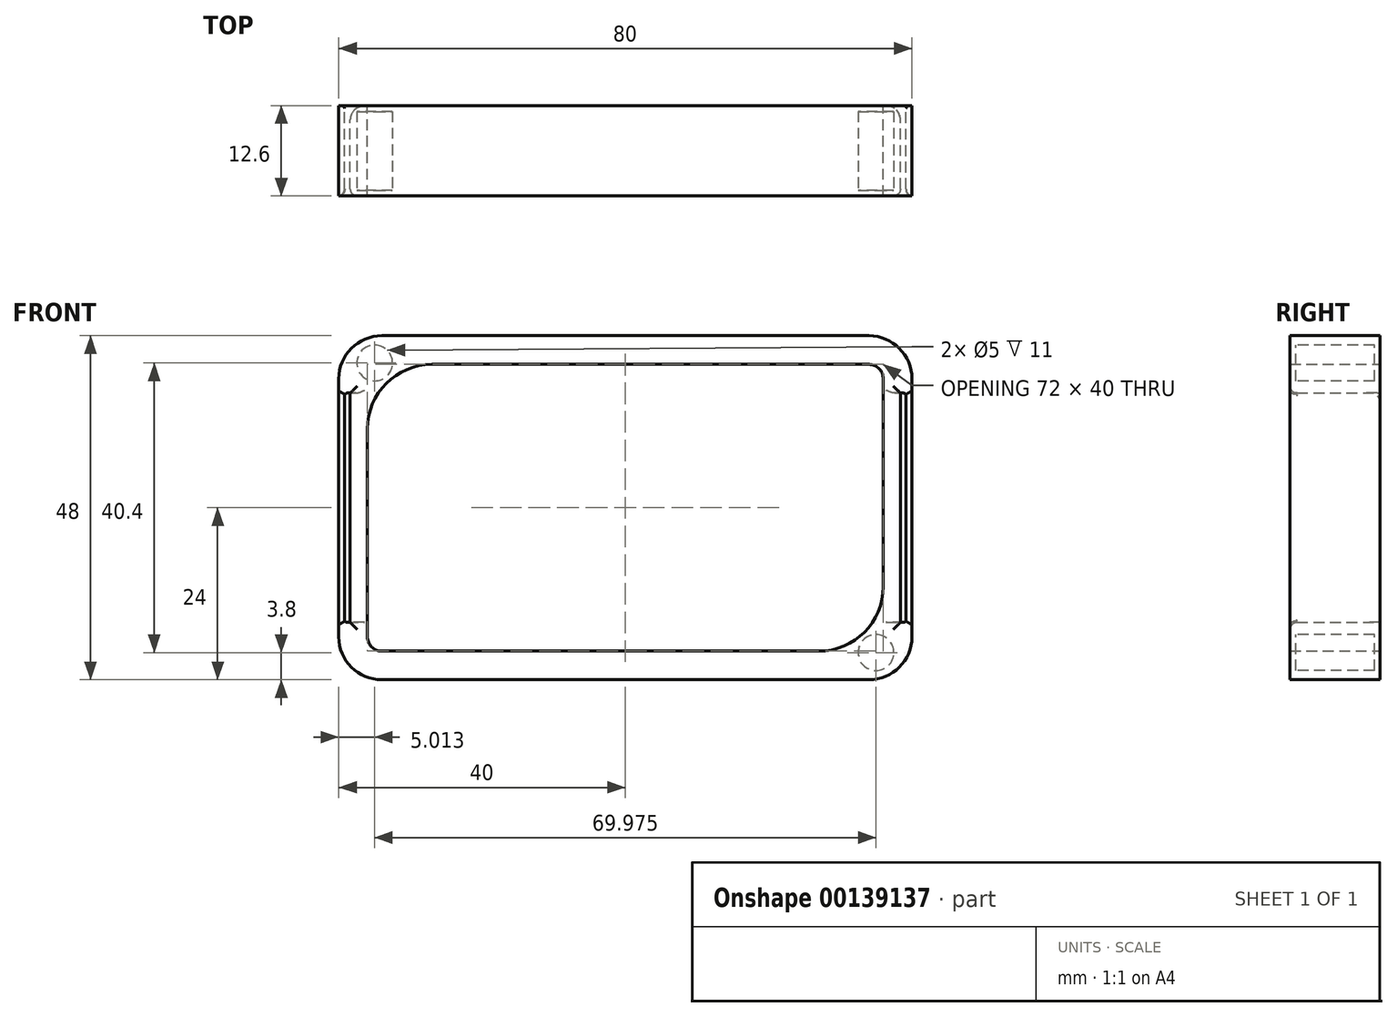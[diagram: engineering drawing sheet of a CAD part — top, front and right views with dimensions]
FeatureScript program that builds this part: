
annotation { "Feature Type Name" : "Feature", "Feature Type Description" : "" }
export const myFeature = defineFeature(function(context is Context, id is Id, definition is map)
    precondition{}
    {
        {
            var Q0;
            Q0=qCreatedBy(makeId("Front.planeOp"),FACE);
            var sketch = newSketch(context, id + "F0", { "sketchPlane" : qUnion([Q0])});
            skLineSegment(sketch, "E0.bottom", {"start": v(-34, 24) * mm, "end": v(34, 24) * mm});
            skLineSegment(sketch, "E0.top", {"start": v(-34, -24) * mm, "end": v(34, -24) * mm});
            skLineSegment(sketch, "E0.left", {"start": v(-40, 18) * mm, "end": v(-40, -18) * mm});
            skLineSegment(sketch, "E0.right", {"start": v(40, 18) * mm, "end": v(40, -18) * mm});
            skPoint(sketch, "E1", {"position": v(0, 24) * mm});
            skPoint(sketch, "E2", {"position": v(-40, 0) * mm});
            skPoint(sketch, "E3.visualSharp", {"position": v(-40, 24) * mm});
            skArc(sketch, "E3.filletArc", {"start": v(-34, 24) * mm, "mid": v(-38.24, 22.24) * mm, "end": v(-40, 18) * mm});
            skPoint(sketch, "E4.visualSharp", {"position": v(40, 24) * mm});
            skArc(sketch, "E4.filletArc", {"start": v(40, 18) * mm, "mid": v(38.24, 22.24) * mm, "end": v(34, 24) * mm});
            skPoint(sketch, "E5.visualSharp", {"position": v(40, -24) * mm});
            skArc(sketch, "E5.filletArc", {"start": v(34, -24) * mm, "mid": v(38.24, -22.24) * mm, "end": v(40, -18) * mm});
            skPoint(sketch, "E6.visualSharp", {"position": v(-40, -24) * mm});
            skArc(sketch, "E6.filletArc", {"start": v(-40, -18) * mm, "mid": v(-38.24, -22.24) * mm, "end": v(-34, -24) * mm});
            skLineSegment(sketch, "E7.0", {"start": v(-27, 20) * mm, "end": v(34, 20) * mm});
            skLineSegment(sketch, "E7.1", {"start": v(-36, 11) * mm, "end": v(-36, -18) * mm});
            skLineSegment(sketch, "E7.2", {"start": v(-34, -20) * mm, "end": v(27, -20) * mm});
            skLineSegment(sketch, "E7.3", {"start": v(36, 18) * mm, "end": v(36, -11) * mm});
            skPoint(sketch, "E8.visualSharp", {"position": v(36, 20) * mm});
            skArc(sketch, "E8.filletArc", {"start": v(36, 18) * mm, "mid": v(35.41, 19.41) * mm, "end": v(34, 20) * mm});
            skPoint(sketch, "E9.visualSharp", {"position": v(36, -20) * mm});
            skPoint(sketch, "E10.visualSharp", {"position": v(-36, -20) * mm});
            skArc(sketch, "E10.filletArc", {"start": v(-36, -18) * mm, "mid": v(-35.41, -19.41) * mm, "end": v(-34, -20) * mm});
            skPoint(sketch, "E11.visualSharp", {"position": v(-36, 20) * mm});
            skArc(sketch, "E12.filletArc", {"start": v(-27, 20) * mm, "mid": v(-33.36, 17.36) * mm, "end": v(-36, 11) * mm});
            skArc(sketch, "E13.filletArc", {"start": v(27, -20) * mm, "mid": v(33.36, -17.36) * mm, "end": v(36, -11) * mm});
            skLineSegment(sketch, "E14.bottom", {"start": v(-39.2, 16) * mm, "end": v(-38.4, 16) * mm});
            skLineSegment(sketch, "E14.top", {"start": v(-39.2, -16) * mm, "end": v(-38.4, -16) * mm});
            skLineSegment(sketch, "E14.left", {"start": v(-39.2, 16) * mm, "end": v(-39.2, -16) * mm});
            skLineSegment(sketch, "E14.right", {"start": v(-38.4, 16) * mm, "end": v(-38.4, -16) * mm});
            skLineSegment(sketch, "E15.MirrorCS", {"start": v(38.4, 16) * mm, "end": v(38.4, -16) * mm});
            skLineSegment(sketch, "E16.MirrorCS", {"start": v(39.2, 16) * mm, "end": v(38.4, 16) * mm});
            skLineSegment(sketch, "E17.MirrorCS", {"start": v(39.2, 16) * mm, "end": v(39.2, -16) * mm});
            skLineSegment(sketch, "E18.MirrorCS", {"start": v(39.2, -16) * mm, "end": v(38.4, -16) * mm});
            skPoint(sketch, "E19", {"position": v(-39.2, 0) * mm});
            skPoint(sketch, "E20", {"position": v(39.2, 0) * mm});
            skSolve(sketch);
        }
        {
            var Q0;
            Q0=makeQuery(id+"F0.imprint","IMPRINT",FACE,{"disambiguationData":[TD([[makeQuery(id+"F0.imprint","IMPRINT",EDGE,{"derivedFrom":sQuery(id+"F0.wireOp",EDGE,"E0.bottom")}),-1.0]])]});
            var Q1;
            {var subQ0=sQuery(id+"F0.wireOp",EDGE,"E11.filletArc");Q1=makeQuery(id+"F0.imprint","IMPRINT",FACE,{"disambiguationData":[TD([[makeQuery(id+"F0.imprint","IMPRINT",EDGE,{"derivedFrom":subQ0}),1.0]])]});}
            var Q2;
            {var subQ0=sQuery(id+"F0.wireOp",EDGE,"E11.filletArc");Q2=makeQuery(id+"F0.imprint","IMPRINT",FACE,{"disambiguationData":[TD([[makeQuery(id+"F0.imprint","IMPRINT",EDGE,{"derivedFrom":subQ0}),-1.0]])]});}
            extrude(context, id + "F1", {"entities" : qUnion([Q0, Q1, Q2]), "endBound" : BoundingType.SYMMETRIC, "depth" : 12.6 * mm});
        }
        {
            var Q0;
            Q0=makeQuery(id+"F1.opExtrude","CAP_FACE",FACE,{"disambiguationData":[OSD([sQuery(id+"F0.wireOp",EDGE,"E0.bottom"),sQuery(id+"F0.wireOp",EDGE,"E0.top"),sQuery(id+"F0.wireOp",EDGE,"E0.left"),sQuery(id+"F0.wireOp",EDGE,"E0.right"),sQuery(id+"F0.wireOp",EDGE,"E3.filletArc"),sQuery(id+"F0.wireOp",EDGE,"E4.filletArc"),sQuery(id+"F0.wireOp",EDGE,"E5.filletArc"),sQuery(id+"F0.wireOp",EDGE,"E6.filletArc"),sQuery(id+"F0.wireOp",EDGE,"E7.0"),sQuery(id+"F0.wireOp",EDGE,"E7.1"),sQuery(id+"F0.wireOp",EDGE,"E7.2"),sQuery(id+"F0.wireOp",EDGE,"E7.3"),sQuery(id+"F0.wireOp",EDGE,"E8.filletArc"),sQuery(id+"F0.wireOp",EDGE,"E9.filletArc"),sQuery(id+"F0.wireOp",EDGE,"E10.filletArc"),sQuery(id+"F0.wireOp",EDGE,"E11.filletArc")])],"isStart":false});
            cPlane(context, id + "F2", {"entities" : qUnion([Q0]), "cplaneType" : CPlaneType.OFFSET, "offset" : 0.8 * mm, "oppositeDirection" : true, "width" : 150 * mm, "height" : 150 * mm});
        }
        {
            var Q0;
            Q0=qCreatedBy(id+"F2.planeOp",FACE);
            var sketch = newSketch(context, id + "F3", { "sketchPlane" : qUnion([Q0])});
            skPoint(sketch, "E21", {"position": v(-34.99, 20.2) * mm});
            skLineSegment(sketch, "E22", {"start": v(-34.99, 20.2) * mm, "end": v(34.99, -20.2) * mm, "construction": true});
            skCircle(sketch, "E23", {"center": v(-34.99, 20.2) * mm, "radius": 2.5 * mm});
            skCircle(sketch, "E24", {"center": v(34.99, -20.2) * mm, "radius": 2.5 * mm});
            skSolve(sketch);
        }
        {
            var Q0;
            Q0=qSketchRegion(id+"F3",true);
            extrude(context, id + "F4", {"entities" : qUnion([Q0]), "operationType" : NewBodyOperationType.REMOVE, "oppositeDirection" : true, "depth" : 11 * mm});
        }
        {
            var Q0;
            Q0=makeQuery(id+"F1.opExtrude","CAP_EDGE",EDGE,{"disambiguationData":[OSD([sQuery(id+"F0.wireOp",EDGE,"E14.right")])],"isStart":true});
            var Q1;
            Q1=makeQuery(id+"F1.opExtrude","CAP_EDGE",EDGE,{"disambiguationData":[OSD([sQuery(id+"F0.wireOp",EDGE,"E15.MirrorCS")])],"isStart":true});
            fillet(context, id + "F5", {"entities" : qUnion([Q0, Q1]), "radius" : 2 * mm, "allowEdgeOverflow" : false});
        }
        {
            var Q0;
            Q0=makeQuery(id+"F1.opExtrude","SWEPT_EDGE",EDGE,{"disambiguationData":[OSD([sQuery(id+"F0.wireOp",EDGE,"E14.bottom"),sQuery(id+"F0.wireOp",EDGE,"E14.left")])]});
            var Q1;
            Q1=makeQuery(id+"F1.opExtrude","SWEPT_EDGE",EDGE,{"disambiguationData":[OSD([sQuery(id+"F0.wireOp",EDGE,"E14.top"),sQuery(id+"F0.wireOp",EDGE,"E14.left")])]});
            var Q2;
            Q2=makeQuery(id+"F1.opExtrude","SWEPT_EDGE",EDGE,{"disambiguationData":[OSD([sQuery(id+"F0.wireOp",EDGE,"E17.MirrorCS"),sQuery(id+"F0.wireOp",EDGE,"E18.MirrorCS")])]});
            var Q3;
            Q3=makeQuery(id+"F1.opExtrude","SWEPT_EDGE",EDGE,{"disambiguationData":[OSD([sQuery(id+"F0.wireOp",EDGE,"E16.MirrorCS"),sQuery(id+"F0.wireOp",EDGE,"E17.MirrorCS")])]});
            var Q4;
            Q4=makeQuery(id+"F1.opExtrude","CAP_EDGE",EDGE,{"disambiguationData":[OSD([sQuery(id+"F0.wireOp",EDGE,"E16.MirrorCS")])],"isStart":true});
            var Q5;
            Q5=makeQuery(id+"F1.opExtrude","CAP_EDGE",EDGE,{"disambiguationData":[OSD([sQuery(id+"F0.wireOp",EDGE,"E14.bottom")])],"isStart":true});
            fillet(context, id + "F6", {"entities" : qUnion([Q0, Q1, Q2, Q3, Q4, Q5]), "radius" : 0.4 * mm, "tangentPropagation" : true, "allowEdgeOverflow" : false});
        }
        {
            var Q0;
            Q0=makeQuery(id+"F1.opExtrude","CAP_EDGE",EDGE,{"disambiguationData":[OSD([sQuery(id+"F0.wireOp",EDGE,"E15.MirrorCS")])],"isStart":false});
            var Q1;
            Q1=makeQuery(id+"F1.opExtrude","CAP_EDGE",EDGE,{"disambiguationData":[OSD([sQuery(id+"F0.wireOp",EDGE,"E17.MirrorCS")])],"isStart":false});
            var Q2;
            Q2=makeQuery(id+"F1.opExtrude","CAP_EDGE",EDGE,{"disambiguationData":[OSD([sQuery(id+"F0.wireOp",EDGE,"E14.right")])],"isStart":false});
            var Q3;
            Q3=makeQuery(id+"F1.opExtrude","CAP_EDGE",EDGE,{"disambiguationData":[OSD([sQuery(id+"F0.wireOp",EDGE,"E14.left")])],"isStart":false});
            fillet(context, id + "F7", {"entities" : qUnion([Q0, Q1, Q2, Q3]), "radius" : 1 * mm, "tangentPropagation" : true, "allowEdgeOverflow" : false});
        }
    });
